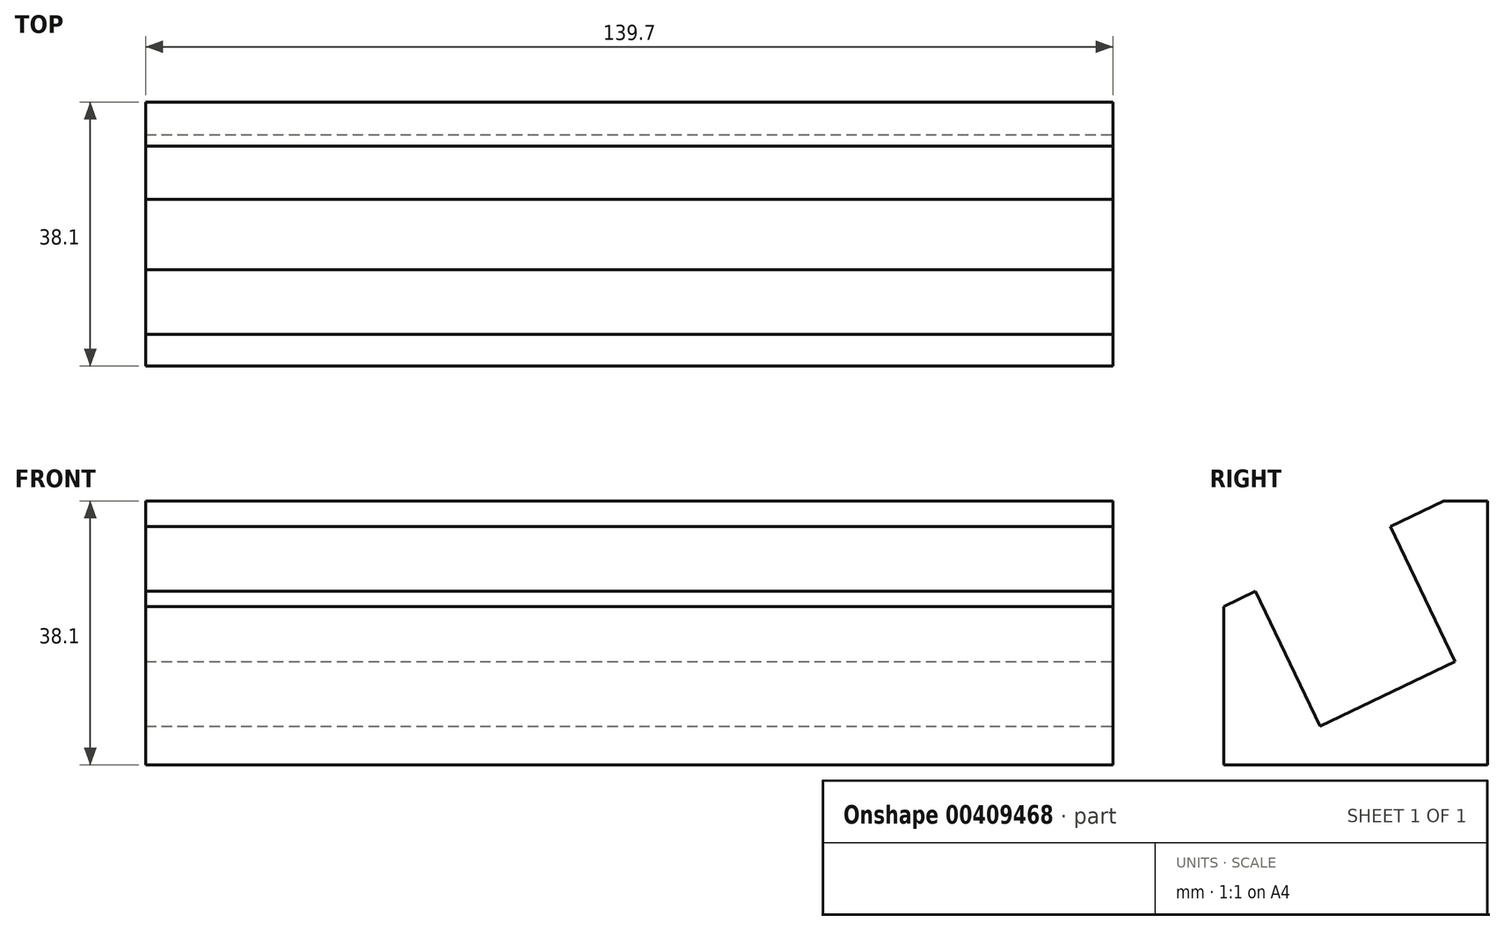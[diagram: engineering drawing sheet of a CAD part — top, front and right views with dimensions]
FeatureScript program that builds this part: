
annotation { "Feature Type Name" : "Feature", "Feature Type Description" : "" }
export const myFeature = defineFeature(function(context is Context, id is Id, definition is map)
    precondition{}
    {
        {
            var Q0;
            Q0=qCreatedBy(makeId("Top.planeOp"),FACE);
            var sketch = newSketch(context, id + "F0", { "sketchPlane" : qUnion([Q0])});
            skLineSegment(sketch, "E0.bottom", {"start": v(69.85, 19.05) * mm, "end": v(-69.85, 19.05) * mm});
            skLineSegment(sketch, "E0.top", {"start": v(69.85, -19.05) * mm, "end": v(-69.85, -19.05) * mm});
            skLineSegment(sketch, "E0.left", {"start": v(69.85, 19.05) * mm, "end": v(69.85, -19.05) * mm});
            skLineSegment(sketch, "E0.right", {"start": v(-69.85, 19.05) * mm, "end": v(-69.85, -19.05) * mm});
            skPoint(sketch, "E0.middle", {"position": v(0, 0) * mm});
            skSolve(sketch);
        }
        {
            var Q0;
            Q0 = qSketchRegion(id + "F0", true);
            extrude(context, id + "F1", {"entities" : qUnion([Q0]), "depth" : 38.1 * mm});
        }
        {
            var Q0;
            Q0=makeQuery(id+"F1.opExtrude","SWEPT_FACE",FACE,{"disambiguationData":[OSD([sQuery(id+"F0.wireOp",EDGE,"E0.left")])]});
            var sketch = newSketch(context, id + "F2", { "sketchPlane" : qUnion([Q0])});
            skLineSegment(sketch, "E1", {"start": v(12.7, 38.1) * mm, "end": v(-19.05, 22.86) * mm});
            skSolve(sketch);
        }
        {
            var Q0;
            Q0 = qSketchRegion(id + "F2", true);
            var Q1;
            {var subQ0=sQuery(id+"F2.wireOp",EDGE,"E1");Q1=makeQuery(id+"F2.imprint","IMPRINT",FACE,{"disambiguationData":[TD([[makeQuery(id+"F2.imprint","IMPRINT",EDGE,{"derivedFrom":subQ0}),-1.0]])]});}
            extrude(context, id + "F3", {"entities" : qUnion([Q0, Q1]), "operationType" : NewBodyOperationType.REMOVE, "endBound" : BoundingType.THROUGH_ALL, "oppositeDirection" : true, "depth" : 25.4 * mm});
        }
        {
            var Q0;
            Q0=makeQuery(id+"F1.opExtrude","SWEPT_FACE",FACE,{"disambiguationData":[OSD([sQuery(id+"F0.wireOp",EDGE,"E0.left")])]});
            var sketch = newSketch(context, id + "F4", { "sketchPlane" : qUnion([Q0])});
            skLineSegment(sketch, "E2", {"start": v(5, 34.4) * mm, "end": v(14.34, 14.94) * mm});
            skLineSegment(sketch, "E3", {"start": v(14.34, 14.94) * mm, "end": v(-5.13, 5.6) * mm});
            skLineSegment(sketch, "E4", {"start": v(-5.13, 5.6) * mm, "end": v(-14.47, 25.06) * mm});
            skSolve(sketch);
        }
        {
            var Q0;
            {var subQ0=sQuery(id+"F4.wireOp",EDGE,"E2");Q0=makeQuery(id+"F4.imprint","IMPRINT",FACE,{"disambiguationData":[TD([[makeQuery(id+"F4.imprint","IMPRINT",EDGE,{"derivedFrom":subQ0}),-1.0]])]});}
            extrude(context, id + "F5", {"entities" : qUnion([Q0]), "operationType" : NewBodyOperationType.REMOVE, "endBound" : BoundingType.THROUGH_ALL, "oppositeDirection" : true, "depth" : 25.4 * mm});
        }
    });
